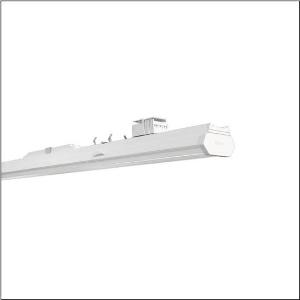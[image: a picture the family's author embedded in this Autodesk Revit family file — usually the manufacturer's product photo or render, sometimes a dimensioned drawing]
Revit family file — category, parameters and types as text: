
# Revit family: licross_r__21_protected_mo_52ts12cn67xf_4b2a
name_source: partatom
category: Lighting Fixtures
units: mm (PartAtom-declared; Revit-internal decimal feet)

## family parameters
Cut with Voids When Loaded = No
Host = Face
Light Source = No
Part Type = Normal
Room Calculation Point = No
Round Connector Dimension = Use Diameter
Shared = No

## types (1)
- --- (1 x LED, 7470 lm, 48.5 W, 6500K)
    Apparent Load = 49 VA
    CIE Flux Codes = 54 82 95 97 100
    Color Rendering = 80
    Color Temperature = 6500K
    Default Elevation = 1800 mm
    Description = Licross® 21 Protected MO, luminaire insert, of sheet steel, galvanised, coil coated, white, length: 1.500mm, width: 90mm, height: 101mm, LED rated luminous flux: 7.460lm, light colour: 865, control gear: ON/OFF Multilumen, CLOi, control gear: ECG Multilumen, with plug, 3-pole, with phase selection, mains connection: 220..240V, AC, 50/60Hz, start of lifetime: 49W, end of service life: 55W, halogen-free wiring, primary optical cover: cover, of PMMA, light emission: direct distribution, primary light characteristic: symmetric, protection rating (complete): IP50, insulation class (complete): insulation class I (protective earthing), certification: CE, ENEC, VDE, UKCA, protection symbol: D if used in an environment with conductive dust loads with corresponding accessories, impact resistance: IK06, permissible ambient temperature for indoor applications: -35..+45°C, corresponds to IFS (International Featured Standards) requirements for safety and quality in the food industry, reducing of maximum allowable ambient temperature of 5°C with ceiling mounting, LABS conformity tested according to VDMA 24364:2018-05, packaging unit: 1 piece
    Height = 92 mm
    Lamp = 1 x LED
    Lamp Light Flux = 7470 lm
    Lamp Power = 48.5 W
    Lamp count = 1
    Length = 1500 mm
    Luminous efficacy = 154 lm/W
    Manufacturer = Siteco
    ModVariant = No
    Model = 52TS12CN67XF
    Mounting Place = Ceiling
    Mounting Type = Pendant
    Number of Poles = 1
    OnlyDefault = Yes
    Power Factor = 1
    Product Name = Licross® 21 Protected MO
    Product group = luminaire insert
    ProductGroupID = 901
    Protection Class = Protection class I
    Protection Degree = IP 50
    RLX_Detail_Level = 1
    RLX_Emergency_Light_Flux = 0 lm
    RLX_Emergency_Type = 0
    RLX_Emergency_Type_DB = No
    RlxData = <blob elided: 21969 chars, md5=e9083b54>
    Socket = socket
    Standby Power = 0 W
    System Light Flux = 7470 lm
    System Power = 49 W
    Type Comments = factory setting: luminous flux: 100 % | (A | C | E) | 117 mA
    Type Image = l_1256145.jpg
    URL = http://relux.com
    VarID = @adj_149649
    Voltage = 0 V
    Weight = 0.00 kg
    Width = 88 mm

## geometry (parser evidence)
native form markers: Blend x4, Sweep x12
no freeform markers — native parametric forms only
